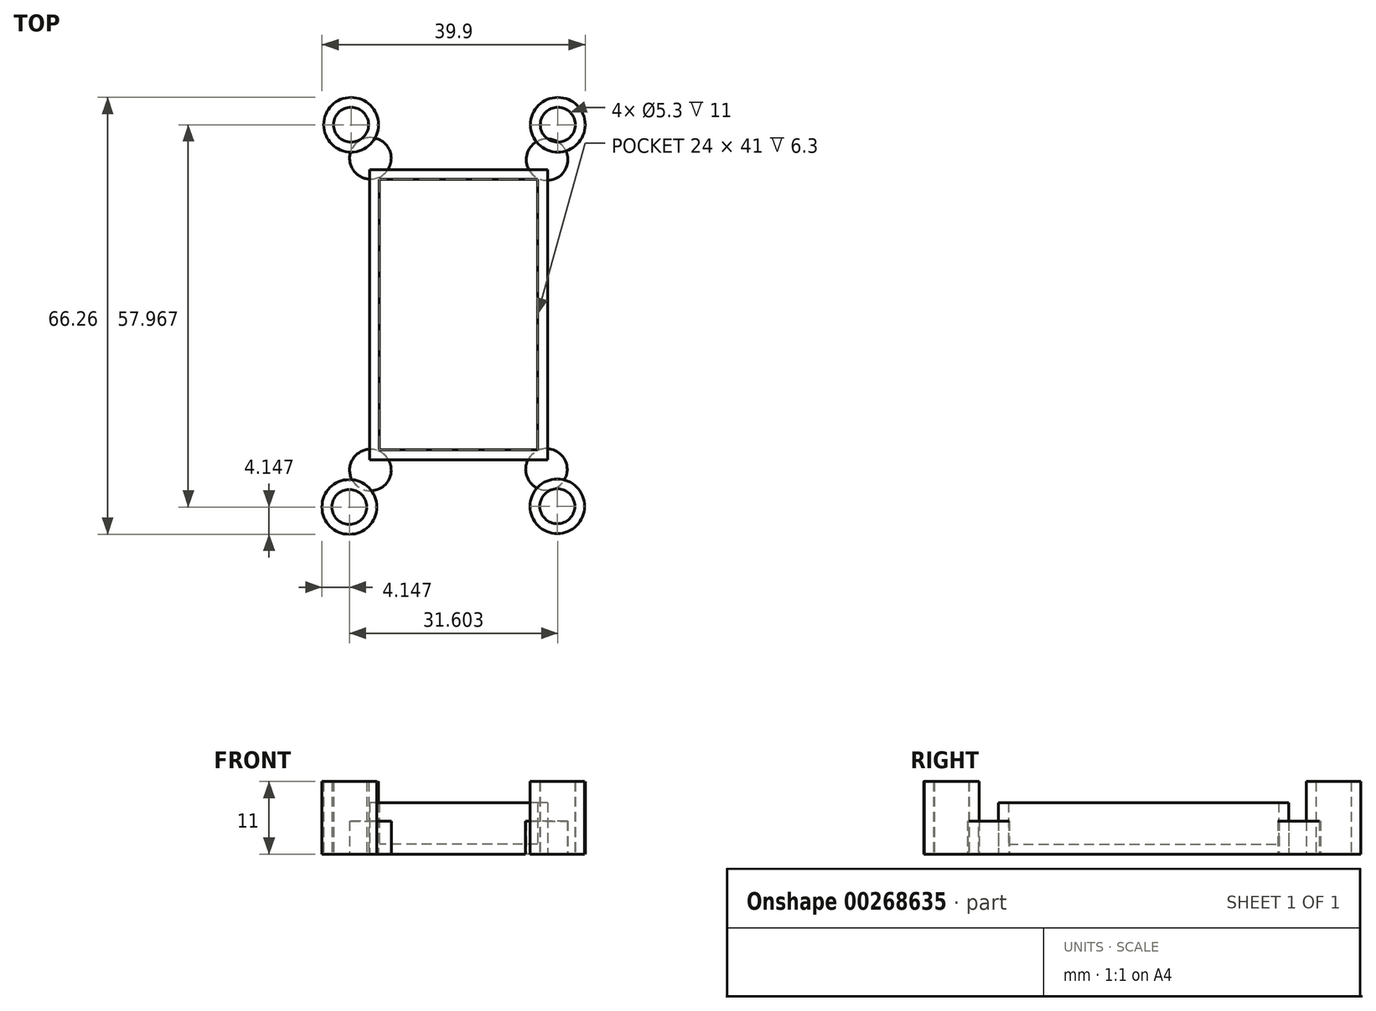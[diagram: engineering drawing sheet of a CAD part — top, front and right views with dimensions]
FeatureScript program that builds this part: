
annotation { "Feature Type Name" : "Feature", "Feature Type Description" : "" }
export const myFeature = defineFeature(function(context is Context, id is Id, definition is map)
    precondition{}
    {
        {
            var Q0;
            Q0=qCreatedBy(makeId("Top.planeOp"),FACE);
            var sketch = newSketch(context, id + "F0", { "sketchPlane" : qUnion([Q0])});
            skLineSegment(sketch, "E0.bottom", {"start": v(12, -20.5) * mm, "end": v(-12, -20.5) * mm});
            skLineSegment(sketch, "E0.top", {"start": v(12, 20.5) * mm, "end": v(-12, 20.5) * mm});
            skLineSegment(sketch, "E0.left", {"start": v(12, -20.5) * mm, "end": v(12, 20.5) * mm});
            skLineSegment(sketch, "E0.right", {"start": v(-12, -20.5) * mm, "end": v(-12, 20.5) * mm});
            skPoint(sketch, "E0.middle", {"position": v(0, 0) * mm});
            skLineSegment(sketch, "E1.bottom", {"start": v(13.5, -22) * mm, "end": v(-13.5, -22) * mm});
            skLineSegment(sketch, "E1.top", {"start": v(13.5, 22) * mm, "end": v(-13.5, 22) * mm});
            skLineSegment(sketch, "E1.left", {"start": v(13.5, -22) * mm, "end": v(13.5, 22) * mm});
            skLineSegment(sketch, "E1.right", {"start": v(-13.5, -22) * mm, "end": v(-13.5, 22) * mm});
            skSolve(sketch);
        }
        {
            var Q0;
            Q0=qCreatedBy(makeId("Top.planeOp"),FACE);
            var sketch = newSketch(context, id + "F1", { "sketchPlane" : qUnion([Q0])});
            skCircle(sketch, "E2", {"center": v(-16.3, 29.1) * mm, "radius": 2.65 * mm});
            skLineSegment(sketch, "E3", {"start": v(22.9, 31.9) * mm, "end": v(-45.27, 31.9) * mm, "construction": true});
            skLineSegment(sketch, "E4", {"start": v(26.43, -31.5) * mm, "end": v(-30.34, -31.5) * mm, "construction": true});
            skLineSegment(sketch, "E5", {"start": v(17.76, 35.09) * mm, "end": v(17.76, -40.54) * mm, "construction": true});
            skLineSegment(sketch, "E6", {"start": v(-19.14, 34.5) * mm, "end": v(-19.14, -35.83) * mm, "construction": true});
            skCircle(sketch, "E7", {"center": v(-16.3, 29.1) * mm, "radius": 4.15 * mm});
            skCircle(sketch, "E8", {"center": v(15.04, 29.1) * mm, "radius": 2.65 * mm});
            skCircle(sketch, "E9", {"center": v(15.04, 29.1) * mm, "radius": 4.15 * mm});
            skCircle(sketch, "E10", {"center": v(14.97, -28.77) * mm, "radius": 2.65 * mm});
            skCircle(sketch, "E11", {"center": v(14.97, -28.77) * mm, "radius": 4.15 * mm});
            skCircle(sketch, "E12", {"center": v(-16.56, -28.87) * mm, "radius": 2.65 * mm});
            skCircle(sketch, "E13", {"center": v(-16.56, -28.87) * mm, "radius": 4.15 * mm});
            skSolve(sketch);
        }
        {
            var Q0;
            Q0=makeQuery(id+"F0.imprint","IMPRINT",FACE,{"disambiguationData":[TD([[makeQuery(id+"F0.imprint","IMPRINT",EDGE,{"derivedFrom":sQuery(id+"F0.wireOp",EDGE,"E0.bottom")}),1.0]])]});
            extrude(context, id + "F2", {"entities" : qUnion([Q0]), "depth" : 7.8 * mm});
        }
        {
            var Q0;
            Q0=makeQuery(id+"F1.imprint","IMPRINT",FACE,{"disambiguationData":[TD([[makeQuery(id+"F1.imprint","IMPRINT",EDGE,{"derivedFrom":sQuery(id+"F1.wireOp",EDGE,"E2")}),1.0]])]});
            var Q1;
            Q1=makeQuery(id+"F1.imprint","IMPRINT",FACE,{"disambiguationData":[TD([[makeQuery(id+"F1.imprint","IMPRINT",EDGE,{"derivedFrom":sQuery(id+"F1.wireOp",EDGE,"E2")}),-1.0]])]});
            var Q2;
            Q2=makeQuery(id+"F1.imprint","IMPRINT",FACE,{"disambiguationData":[TD([[makeQuery(id+"F1.imprint","IMPRINT",EDGE,{"derivedFrom":sQuery(id+"F1.wireOp",EDGE,"E8")}),1.0]])]});
            var Q3;
            Q3=makeQuery(id+"F1.imprint","IMPRINT",FACE,{"disambiguationData":[TD([[makeQuery(id+"F1.imprint","IMPRINT",EDGE,{"derivedFrom":sQuery(id+"F1.wireOp",EDGE,"E8")}),-1.0]])]});
            var Q4;
            Q4=makeQuery(id+"F1.imprint","IMPRINT",FACE,{"disambiguationData":[TD([[makeQuery(id+"F1.imprint","IMPRINT",EDGE,{"derivedFrom":sQuery(id+"F1.wireOp",EDGE,"E12")}),1.0]])]});
            var Q5;
            Q5=makeQuery(id+"F1.imprint","IMPRINT",FACE,{"disambiguationData":[TD([[makeQuery(id+"F1.imprint","IMPRINT",EDGE,{"derivedFrom":sQuery(id+"F1.wireOp",EDGE,"E12")}),-1.0]])]});
            var Q6;
            Q6=makeQuery(id+"F1.imprint","IMPRINT",FACE,{"disambiguationData":[TD([[makeQuery(id+"F1.imprint","IMPRINT",EDGE,{"derivedFrom":sQuery(id+"F1.wireOp",EDGE,"E10")}),1.0]])]});
            var Q7;
            Q7=makeQuery(id+"F1.imprint","IMPRINT",FACE,{"disambiguationData":[TD([[makeQuery(id+"F1.imprint","IMPRINT",EDGE,{"derivedFrom":sQuery(id+"F1.wireOp",EDGE,"E10")}),-1.0]])]});
            extrude(context, id + "F3", {"entities" : qUnion([Q0, Q1, Q2, Q3, Q4, Q5, Q6, Q7]), "depth" : 11 * mm});
        }
        {
            var Q0;
            Q0=sQuery(id+"F1.wireOp",VERTEX,"E7.center");
            var Q1;
            Q1=sQuery(id+"F1.wireOp",VERTEX,"E9.center");
            var Q2;
            Q2=sQuery(id+"F1.wireOp",VERTEX,"E10.center");
            var Q3;
            Q3=sQuery(id+"F1.wireOp",VERTEX,"E13.center");
            var Q4;
            Q4=makeQuery(id+"F3.opExtrude","SWEPT_BODY",BODY,{"disambiguationData":[OSD([sQuery(id+"F1.wireOp",EDGE,"E7")])]});
            var Q5;
            Q5=makeQuery(id+"F3.opExtrude","SWEPT_BODY",BODY,{"disambiguationData":[OSD([sQuery(id+"F1.wireOp",EDGE,"E9")])]});
            var Q6;
            Q6=makeQuery(id+"F3.opExtrude","SWEPT_BODY",BODY,{"disambiguationData":[OSD([sQuery(id+"F1.wireOp",EDGE,"E11")])]});
            var Q7;
            Q7=makeQuery(id+"F3.opExtrude","SWEPT_BODY",BODY,{"disambiguationData":[OSD([sQuery(id+"F1.wireOp",EDGE,"E13")])]});
            hole(context, id + "F4", {"style" : HoleStyle.SIMPLE, "endStyle" : HoleEndStyle.THROUGH, "oppositeDirection" : true, "holeDiameter" : 5.3 * mm, "tappedDepth" : 12 * mm, "tapClearance" : 3, "locations" : qUnion([Q0, Q1, Q2, Q3]), "scope" : qUnion([Q4, Q5, Q6, Q7])});
        }
        {
            var Q0;
            Q0=makeQuery(id+"F2.opExtrude","SWEPT_FACE",FACE,{"disambiguationData":[OSD([sQuery(id+"F0.wireOp",EDGE,"E0.right")])]});
            extrude(context, id + "F5", {"entities" : qUnion([Q0]), "operationType" : NewBodyOperationType.ADD, "depth" : 25 * mm});
        }
        {
            var Q0;
            {var subQ0=sQuery(id+"F0.wireOp",EDGE,"E0.right");Q0=makeQuery(id+"F5.boolean.opBoolean","MERGE",FACE,{"derivedFrom":[makeQuery(id+"F2.opExtrude","CAP_FACE",FACE,{"disambiguationData":[OSD([sQuery(id+"F0.wireOp",EDGE,"E0.bottom"),sQuery(id+"F0.wireOp",EDGE,"E0.top"),sQuery(id+"F0.wireOp",EDGE,"E0.left"),subQ0,sQuery(id+"F0.wireOp",EDGE,"E1.bottom"),sQuery(id+"F0.wireOp",EDGE,"E1.top"),sQuery(id+"F0.wireOp",EDGE,"E1.left"),sQuery(id+"F0.wireOp",EDGE,"E1.right")])],"isStart":false}),makeQuery(id+"F5.opExtrude","SWEPT_FACE",FACE,{"disambiguationData":[OSD([subQ0]),TDD([makeQuery(id+"F2.opExtrude","CAP_EDGE",EDGE,{"disambiguationData":[OSD([subQ0])],"isStart":false})])]})]});}
            shell(context, id + "F6", {"entities" : qUnion([Q0]), "thickness" : 1.5 * mm});
        }
        {
            var Q0;
            Q0=qCreatedBy(makeId("Top.planeOp"),FACE);
            var sketch = newSketch(context, id + "F7", { "sketchPlane" : qUnion([Q0])});
            skCircle(sketch, "E14", {"center": v(-13.36, 23.7) * mm, "radius": 3.15 * mm});
            skCircle(sketch, "E15", {"center": v(13.41, 23.5) * mm, "radius": 3.15 * mm});
            skCircle(sketch, "E16", {"center": v(-13.36, -23.57) * mm, "radius": 3.15 * mm});
            skCircle(sketch, "E17", {"center": v(13.32, -23.48) * mm, "radius": 3.15 * mm});
            skSolve(sketch);
        }
        {
            var Q0;
            Q0=makeQuery(id+"F7.imprint","IMPRINT",FACE,{"disambiguationData":[TD([[makeQuery(id+"F7.imprint","IMPRINT",EDGE,{"derivedFrom":sQuery(id+"F7.wireOp",EDGE,"E15")}),1.0]])]});
            var Q1;
            Q1=makeQuery(id+"F7.imprint","IMPRINT",FACE,{"disambiguationData":[TD([[makeQuery(id+"F7.imprint","IMPRINT",EDGE,{"derivedFrom":sQuery(id+"F7.wireOp",EDGE,"E17")}),1.0]])]});
            var Q2;
            Q2=makeQuery(id+"F7.imprint","IMPRINT",FACE,{"disambiguationData":[TD([[makeQuery(id+"F7.imprint","IMPRINT",EDGE,{"derivedFrom":sQuery(id+"F7.wireOp",EDGE,"E16")}),1.0]])]});
            var Q3;
            Q3=makeQuery(id+"F7.imprint","IMPRINT",FACE,{"disambiguationData":[TD([[makeQuery(id+"F7.imprint","IMPRINT",EDGE,{"derivedFrom":sQuery(id+"F7.wireOp",EDGE,"E14")}),1.0]])]});
            extrude(context, id + "F8", {"entities" : qUnion([Q0, Q1, Q2, Q3]), "depth" : 5 * mm});
        }
        {
            var Q0;
            Q0=makeQuery(id+"F3.opExtrude","SWEPT_BODY",BODY,{"disambiguationData":[OSD([sQuery(id+"F1.wireOp",EDGE,"E7")])]});
            var Q1;
            Q1=makeQuery(id+"F3.opExtrude","SWEPT_BODY",BODY,{"disambiguationData":[OSD([sQuery(id+"F1.wireOp",EDGE,"E9")])]});
            var Q2;
            Q2=makeQuery(id+"F3.opExtrude","SWEPT_BODY",BODY,{"disambiguationData":[OSD([sQuery(id+"F1.wireOp",EDGE,"E11")])]});
            var Q3;
            Q3=makeQuery(id+"F3.opExtrude","SWEPT_BODY",BODY,{"disambiguationData":[OSD([sQuery(id+"F1.wireOp",EDGE,"E13")])]});
            var Q4;
            Q4=qCreatedBy(makeId("Front.planeOp"),FACE);
            transform(context, id + "F9", {"entities" : qUnion([Q0, Q1, Q2, Q3]), "transformType" : TransformType.TRANSLATION_DISTANCE, "transformDirection" : qUnion([Q4]), "distance" : 0.3 * mm, "makeCopy" : false});
        }
    });
